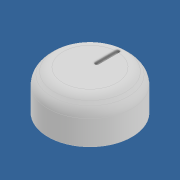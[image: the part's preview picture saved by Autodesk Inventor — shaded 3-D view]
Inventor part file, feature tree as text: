
AUTODESK INVENTOR PART (.ipt)
format: ipt  version: 2020 (Build 240168000, 168)  size: 178,176 bytes
history: native  units: in
note: dims shown in document units (in); Inventor stores cm internally (conversion verified against a paired STEP export)
features: extrude x4, sketch x4, fillet x2, chamfer x1
ambient origin geometry x8: Origin, YZ Plane, XZ Plane, XY Plane, X Axis, Y Axis, Z Axis, Center Point
bodies: Solid1 (feature_tree)
feature tree (11):
  extrude  "Extrusion1"  Depth=0.5118in TaperAngle=0.0deg
  chamfer  "Chamfer1"  Distance=0.1575in Angle=45.0deg
  extrude  "Extrusion2"  Depth=0.3937in
  fillet  "Fillet1"  Radius=0.0787in
  extrude  "Extrusion7"  Depth=0.0394in TaperAngle=0.0deg
  extrude  "Extrusion8"  Depth=0.1969in
  fillet  "Fillet2"  Radius=0.4134in
  sketch  "Sketch1"  dims[d0=1.3386in d1=0.5118in d2=0.0in d3=0.1575in d4=0.0787in d5=45.0deg]
  sketch  "Sketch2"  dims[d6=0.0591in d7=0.3937in d8=0.0787in]
  sketch  "Sketch3"  dims[d9=0.6398in d10=0.0394in d11=0.0in]
  sketch  "Sketch5"  dims[d12=0.0295in d13=0.2362in d41=0.4134in d42=0.0in d45=0.1181in d46=0.0in d50=0.6843in d52=0.6843in d54=0.8589in d55=0.8589in d56=0.1969in d35=0.0197in d36=0.0344in d37=0.0197in d38=0.0344in]
